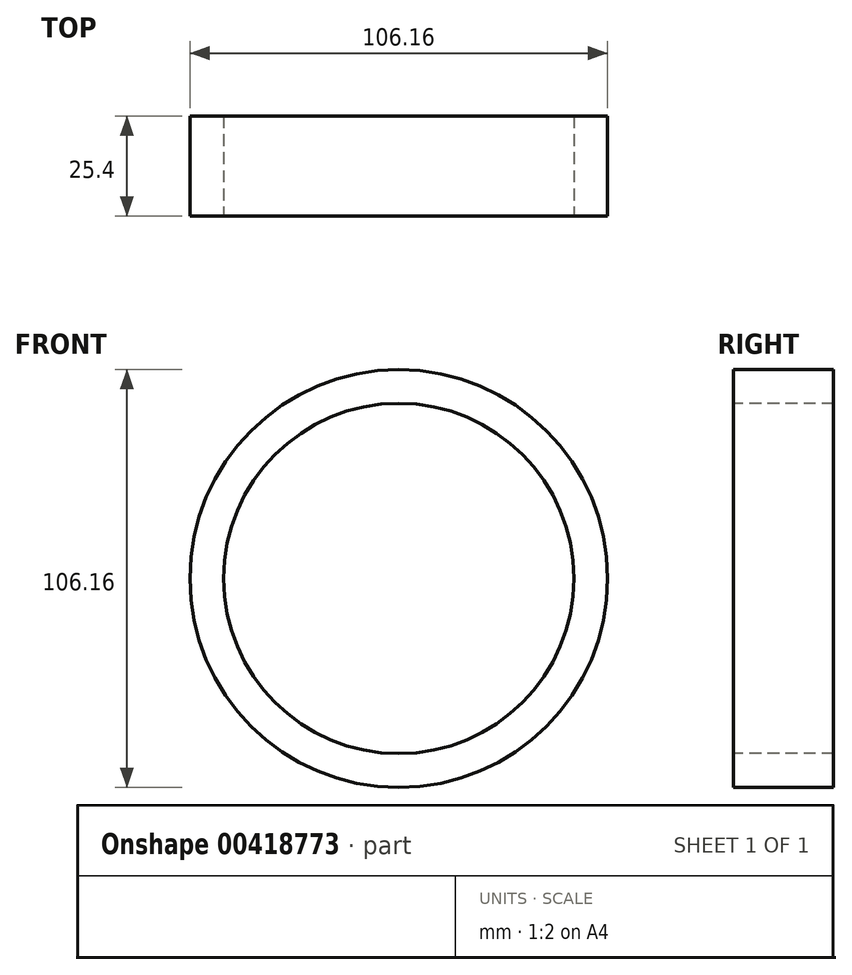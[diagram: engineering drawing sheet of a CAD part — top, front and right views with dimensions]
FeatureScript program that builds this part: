
annotation { "Feature Type Name" : "Feature", "Feature Type Description" : "" }
export const myFeature = defineFeature(function(context is Context, id is Id, definition is map)
    precondition{}
    {
        {
            var Q0;
            Q0=qCreatedBy(makeId("Front.planeOp"),FACE);
            var sketch = newSketch(context, id + "F0", { "sketchPlane" : qUnion([Q0])});
            skCircle(sketch, "E0", {"center": v(0, 0) * mm, "radius": 53.08 * mm});
            skSolve(sketch);
        }
        {
            var Q0;
            Q0=makeQuery(id+"F0.imprint","IMPRINT",FACE,{"disambiguationData":[TD([[makeQuery(id+"F0.imprint","IMPRINT",EDGE,{"derivedFrom":sQuery(id+"F0.wireOp",EDGE,"E0")}),1.0]])]});
            var sketch = newSketch(context, id + "F1", { "sketchPlane" : qUnion([Q0])});
            skCircle(sketch, "E1", {"center": v(0, 0) * mm, "radius": 44.5 * mm});
            skSolve(sketch);
        }
        {
            var Q0;
            Q0=sQuery(id+"F1.wireOp",EDGE,"E1");
            var Q1;
            Q1=sQuery(id+"F0.wireOp",EDGE,"E0");
            extrude(context, id + "F2", {"bodyType" : ToolBodyType.SURFACE, "surfaceEntities" : qUnion([Q0, Q1]), "depth" : 25.4 * mm});
        }
    });
